# Revit family: 2 Towel_Dispenser-Bobrick-TrimLineSeries-B-359033
name_source: partatom
category: Specialty Equipment
units: mm (PartAtom-declared; Revit-internal decimal feet)

## family parameters
Cut with Voids When Loaded = No
Host = Face
OmniClass Number = 23.40.20.21.17
OmniClass Title = Paper Towel Dispensers, Disposal Units
Part Type = Normal
Room Calculation Point = No
Round Connector Dimension = Use Diameter
Shared = Yes

## types (1)
- B-359033
    ADA Compliant = Yes
    Assembly Code = E1090900
    Default Elevation = 50"
    Description = TrimLineSeries™ Recessed Paper Towel Dispenser
    Finish = Stainless Steel-Bobrick-Type 304-Satin
    Height = 17 1/4"
    Installation Type = Recessed
    Length = 4 7/16"
    Manufacturer = Bobrick Washroom Equipment, Inc.
    Material = Stainless Steel-Bobrick-Type 304-Satin
    Model = B-359033
    Price = Prices may vary. Please consult Manufacturer Representative for most up-to-date price list.
    Product Documentation Link = https://www.bobrick.com
    Product Page URL = https://www.bobrick.com
    Revised Date = 11/03/2020
    Specification = Recessed paper towel dispenser shall be Type-304 stainless steel with all-welded construction; exposed surfaces shall have satin finish. Door shall be Type-304, 18 gauge (1.2mm) secured to cabinet with a concealed, full-length stainless steel piano-hinge; and equipped with a stainless steel cable door-swing limiter and a tumbler lock keyed like other Bobrick washroom accessories. Paper towel dispenser shall be 18-8, Type-304, 22-gauge (0.8mm) stainless steel. Capacity: 300 C-fold or 400 multifold paper towels.
    URL = http://www.bobrick.com
    Warranty Documentation Link = https://www.bobrick.com
    Warranty Information = 1 Year Limited Warranty
    Width = 12 3/4"

## geometry (parser evidence)
native form markers: Sweep x3
no freeform markers — native parametric forms only
